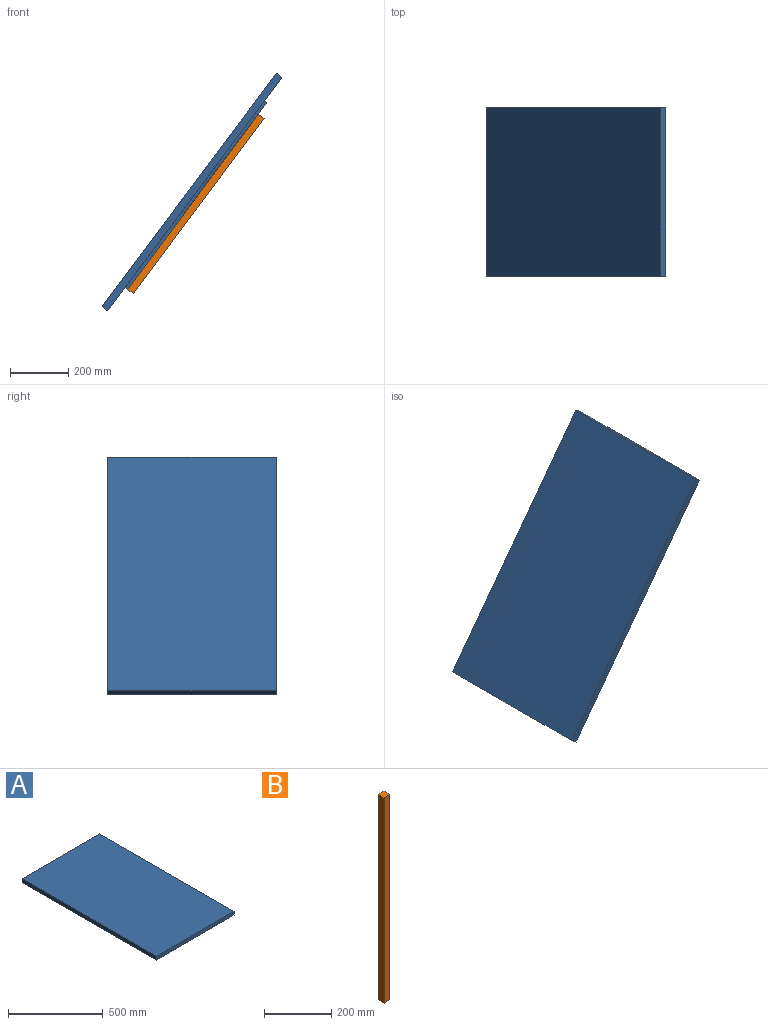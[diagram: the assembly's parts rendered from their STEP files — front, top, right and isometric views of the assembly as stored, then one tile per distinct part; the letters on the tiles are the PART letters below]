
ASSEMBLY  parts=2 mates=1
PART A: 11 faces, bbox 580x1000x35 mm
  f0: plane 580x25mm, normal (0,1,0), area 14500mm2, adj f1,f3,f4,f5
  f1: plane 1000x25mm, normal (-1,0,0), area 25000mm2, adj f0,f2,f4,f5
  f2: plane 580x25mm, normal (0,-1,0), area 14500mm2, adj f1,f3,f4,f5
  f3: plane 1000x25mm, normal (1,0,0), area 25000mm2, adj f0,f2,f4,f5
  f4: plane 1000x580mm, normal (0,0,1), area 580000mm2, adj f0,f1,f2,f3
  f5: plane 1000x580mm, normal (0,0,-1), area 276000mm2, adj f0,f1,f2,f3,f6,f7,f8,f9
  f6: plane 800x10mm, normal (1,0,0), area 8000mm2, adj f5,f7,f9,f10
  f7: plane 380x10mm, normal (0,-1,0), area 3800mm2, adj f5,f6,f8,f10
  f8: plane 800x10mm, normal (-1,0,0), area 8000mm2, adj f5,f7,f9,f10
  f9: plane 380x10mm, normal (0,1,0), area 3800mm2, adj f5,f6,f8,f10
  f10: plane 800x380mm, normal (0,0,-1), area 304000mm2, adj f6,f7,f8,f9
PART B: 6 faces, bbox 25x25x750 mm
  f0: plane 750x25mm, normal (1,0,0), area 18750mm2, adj f1,f3,f4,f5
  f1: plane 25x25mm, normal (0,0,1), area 625mm2, adj f0,f2,f4,f5
  f2: plane 750x25mm, normal (-1,0,0), area 18750mm2, adj f1,f3,f4,f5
  f3: plane 25x25mm, normal (0,0,-1), area 625mm2, adj f0,f2,f4,f5
  f4: plane 750x25mm, normal (0,-1,0), area 18750mm2, adj f0,f1,f2,f3
  f5: plane 750x25mm, normal (0,1,0), area 18750mm2, adj f0,f1,f2,f3
PLACE A rot(axis=(0.41,-0.41,-0.82),101.6deg) t=(-70.71,-96.32,683.88)mm fixed
PLACE B rot(axis=(0,-1,0),143.3deg) t=(122.02,41.39,883.83)mm
MATE revolute A.f8 <-> B.f5  axis (0,1,0) through (-140.63,41.39,573.36)mm
